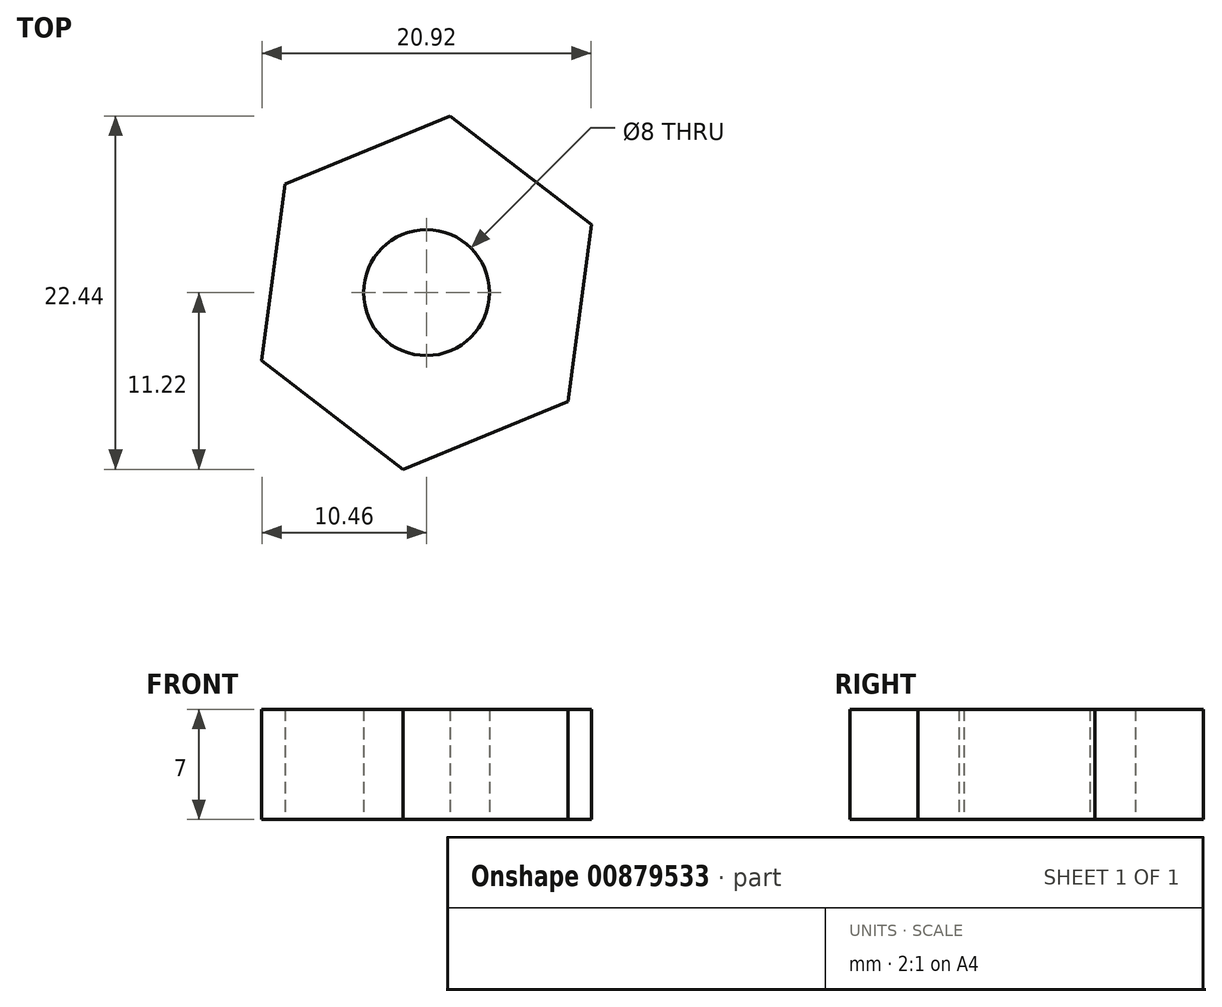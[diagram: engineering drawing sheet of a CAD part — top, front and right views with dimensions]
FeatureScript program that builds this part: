
annotation { "Feature Type Name" : "Feature", "Feature Type Description" : "" }
export const myFeature = defineFeature(function(context is Context, id is Id, definition is map)
    precondition{}
    {
        {
            var Q0;
            Q0=qCreatedBy(makeId("Top.planeOp"),FACE);
            var sketch = newSketch(context, id + "F0", { "sketchPlane" : qUnion([Q0])});
            skCircle(sketch, "E0.cCircle", {"center": v(0, 0) * mm, "radius": 9.8 * mm, "construction": true});
            skLineSegment(sketch, "E0.0", {"start": v(1.5, 11.22) * mm, "end": v(10.46, 4.32) * mm});
            skLineSegment(sketch, "E0.1", {"start": v(10.46, 4.32) * mm, "end": v(8.97, -6.9) * mm});
            skLineSegment(sketch, "E0.2", {"start": v(8.97, -6.9) * mm, "end": v(-1.5, -11.22) * mm});
            skLineSegment(sketch, "E0.3", {"start": v(-1.5, -11.22) * mm, "end": v(-10.46, -4.32) * mm});
            skLineSegment(sketch, "E0.4", {"start": v(-10.46, -4.32) * mm, "end": v(-8.97, 6.9) * mm});
            skLineSegment(sketch, "E0.5", {"start": v(-8.97, 6.9) * mm, "end": v(1.5, 11.22) * mm});
            skPoint(sketch, "E0.0.midPoint", {"position": v(5.98, 7.77) * mm});
            skCircle(sketch, "E1", {"center": v(0, 0) * mm, "radius": 4 * mm});
            skSolve(sketch);
        }
        {
            var Q0;
            Q0=makeQuery(id+"F0.imprint","IMPRINT",FACE,{"disambiguationData":[TD([[makeQuery(id+"F0.imprint","IMPRINT",EDGE,{"derivedFrom":sQuery(id+"F0.wireOp",EDGE,"E0.0")}),-1.0]])]});
            extrude(context, id + "F1", {"entities" : qUnion([Q0]), "depth" : 7 * mm, "offsetDistance" : 25 * mm});
        }
    });
